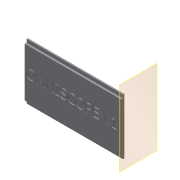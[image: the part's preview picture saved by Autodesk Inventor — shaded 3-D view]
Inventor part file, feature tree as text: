
AUTODESK INVENTOR PART (.ipt)
format: ipt  version: 2019.4 (Build 234330000, 330)  size: 435,200 bytes
history: native  units: mm
features: other x4, plane x3, sketch x3, extrude x3, reference x2, projected_geometry x1
ambient origin geometry x8: Origin, YZ Plane, XZ Plane, XY Plane, X Axis, Y Axis, Z Axis, Center Point
bodies: Volumenkörper1 (feature_tree)
feature tree (16):
  plane  "Arbeitsebene1"
  sketch  "Skizze1"  dims[d5=10.0mm d6=0.0mm d14=0.5mm d15=0.0mm]
  plane  "Arbeitsebene2"
  other  "Arbeitspunkt1"
  plane  "Work Plane3"
  extrude  "Extrusion1"  Depth=0.5mm TaperAngle=0.0deg
  extrude  "Extrusion3"  [1 undecoded]
  extrude  "Extrusion4"  [1 undecoded]
  reference  "Referenz1"
  reference  "Referenz2"
  sketch  "Skizze3"  dims[d16=1.0mm d17=0.0mm]
  sketch  "Sketch4"
  projected_geometry  "Projected Loop2"
  other  "Assembly_Omniscope_v1.iam"
  other  "01_Camera_Module_left_v0:1"
  other  "<userpath>\Documents\Inventor\HITscope\Assembly_Omniscope_v1.iam"
note: 2 required parameter values undecoded (feature->parameter linkage not recoverable at this tier; creation-order binding heuristic only, values carry confidence <= 0.55)
